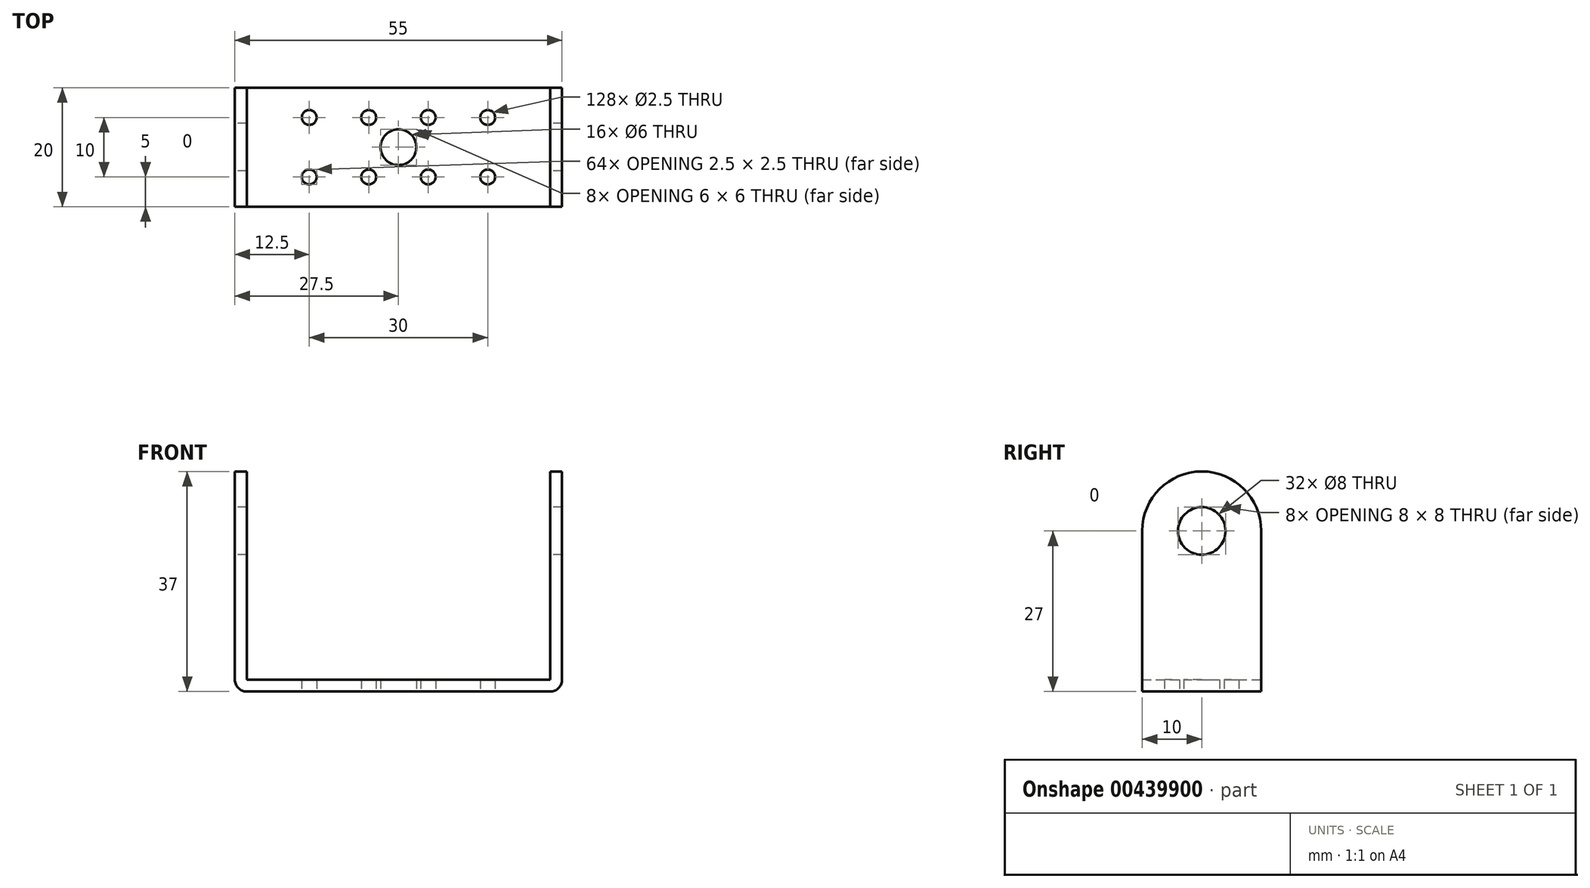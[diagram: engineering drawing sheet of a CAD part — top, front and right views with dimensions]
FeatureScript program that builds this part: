
annotation { "Feature Type Name" : "Feature", "Feature Type Description" : "" }
export const myFeature = defineFeature(function(context is Context, id is Id, definition is map)
    precondition{}
    {
        {
            var Q0;
            Q0=qCreatedBy(makeId("Front.planeOp"),FACE);
            var sketch = newSketch(context, id + "F0", { "sketchPlane" : qUnion([Q0])});
            skLineSegment(sketch, "E0.bottom", {"start": v(-27.5, 37) * mm, "end": v(-25.5, 37) * mm});
            skLineSegment(sketch, "E0.top", {"start": v(-25.5, 2) * mm, "end": v(25.5, 2) * mm});
            skLineSegment(sketch, "E0.left", {"start": v(-25.5, 37) * mm, "end": v(-25.5, 2) * mm});
            skLineSegment(sketch, "E0.right", {"start": v(25.5, 37) * mm, "end": v(25.5, 2) * mm});
            skLineSegment(sketch, "E1", {"start": v(-27.5, 37) * mm, "end": v(-27.5, 0) * mm});
            skLineSegment(sketch, "E2", {"start": v(27.5, 37) * mm, "end": v(27.5, 0) * mm});
            skLineSegment(sketch, "E3.trimOffspring", {"start": v(25.5, 37) * mm, "end": v(27.5, 37) * mm});
            skLineSegment(sketch, "E4", {"start": v(-27.5, 0) * mm, "end": v(27.5, 0) * mm});
            skSolve(sketch);
        }
        {
            var Q0;
            Q0 = qSketchRegion(id + "F0", true);
            extrude(context, id + "F1", {"entities" : qUnion([Q0]), "depth" : 20 * mm});
        }
        {
            var Q0;
            Q0=makeQuery(id+"F1.opExtrude","SWEPT_FACE",FACE,{"disambiguationData":[OSD([sQuery(id+"F0.wireOp",EDGE,"E1")])]});
            var sketch = newSketch(context, id + "F2", { "sketchPlane" : qUnion([Q0])});
            skCircle(sketch, "E5", {"center": v(10, 27) * mm, "radius": 4 * mm});
            skSolve(sketch);
        }
        {
            var Q0;
            Q0 = qSketchRegion(id + "F2", true);
            extrude(context, id + "F3", {"entities" : qUnion([Q0]), "operationType" : NewBodyOperationType.REMOVE, "oppositeDirection" : true, "depth" : 65.2 * mm});
        }
        {
            var Q0;
            Q0=makeQuery(id+"F1.opExtrude","CAP_EDGE",EDGE,{"disambiguationData":[OSD([sQuery(id+"F0.wireOp",EDGE,"E0.bottom")])],"isStart":true});
            var Q1;
            Q1=makeQuery(id+"F1.opExtrude","CAP_EDGE",EDGE,{"disambiguationData":[OSD([sQuery(id+"F0.wireOp",EDGE,"E0.bottom")])],"isStart":false});
            var Q2;
            Q2=makeQuery(id+"F1.opExtrude","CAP_EDGE",EDGE,{"disambiguationData":[OSD([sQuery(id+"F0.wireOp",EDGE,"E3.trimOffspring")])],"isStart":true});
            var Q3;
            Q3=makeQuery(id+"F1.opExtrude","CAP_EDGE",EDGE,{"disambiguationData":[OSD([sQuery(id+"F0.wireOp",EDGE,"E3.trimOffspring")])],"isStart":false});
            fillet(context, id + "F4", {"entities" : qUnion([Q0, Q1, Q2, Q3]), "radius" : 10 * mm, "tangentPropagation" : true, "allowEdgeOverflow" : false});
        }
        {
            var Q0;
            Q0=makeQuery(id+"F1.opExtrude","SWEPT_EDGE",EDGE,{"disambiguationData":[OSD([sQuery(id+"F0.wireOp",EDGE,"E1"),sQuery(id+"F0.wireOp",EDGE,"E4")])]});
            var Q1;
            Q1=makeQuery(id+"F1.opExtrude","SWEPT_EDGE",EDGE,{"disambiguationData":[OSD([sQuery(id+"F0.wireOp",EDGE,"E2"),sQuery(id+"F0.wireOp",EDGE,"E4")])]});
            fillet(context, id + "F5", {"entities" : qUnion([Q0, Q1]), "radius" : 2 * mm, "tangentPropagation" : true, "allowEdgeOverflow" : false});
        }
        {
            var Q0;
            Q0=makeQuery(id+"F1.opExtrude","SWEPT_FACE",FACE,{"disambiguationData":[OSD([sQuery(id+"F0.wireOp",EDGE,"E4")])]});
            var sketch = newSketch(context, id + "F6", { "sketchPlane" : qUnion([Q0])});
            skCircle(sketch, "E6", {"center": v(-15, 15) * mm, "radius": 1.24 * mm});
            skCircle(sketch, "E7.0.1.0", {"center": v(-15, 5) * mm, "radius": 1.24 * mm});
            skCircle(sketch, "E7.1.0.0", {"center": v(-5, 15) * mm, "radius": 1.24 * mm});
            skCircle(sketch, "E7.1.1.0", {"center": v(-5, 5) * mm, "radius": 1.24 * mm});
            skCircle(sketch, "E7.2.0.0", {"center": v(5, 15) * mm, "radius": 1.24 * mm});
            skCircle(sketch, "E7.2.1.0", {"center": v(5, 5) * mm, "radius": 1.24 * mm});
            skCircle(sketch, "E7.3.0.0", {"center": v(15, 15) * mm, "radius": 1.24 * mm});
            skCircle(sketch, "E7.3.1.0", {"center": v(15, 5) * mm, "radius": 1.24 * mm});
            skCircle(sketch, "E8", {"center": v(0, 10) * mm, "radius": 3 * mm});
            skSolve(sketch);
        }
        {
            var Q0;
            Q0=sQuery(id+"F6.wireOp",VERTEX,"E6.center");
            var Q1;
            Q1=sQuery(id+"F6.wireOp",VERTEX,"E7.1.0.0.center");
            var Q2;
            Q2=sQuery(id+"F6.wireOp",VERTEX,"E7.2.0.0.center");
            var Q3;
            Q3=sQuery(id+"F6.wireOp",VERTEX,"E7.3.0.0.center");
            var Q4;
            Q4=sQuery(id+"F6.wireOp",VERTEX,"E7.0.1.0.center");
            var Q5;
            Q5=sQuery(id+"F6.wireOp",VERTEX,"E7.1.1.0.center");
            var Q6;
            Q6=sQuery(id+"F6.wireOp",VERTEX,"E7.2.1.0.center");
            var Q7;
            Q7=sQuery(id+"F6.wireOp",VERTEX,"E7.3.1.0.center");
            var Q8;
            Q8=makeQuery(id+"F1.opExtrude","SWEPT_BODY",BODY,{"disambiguationData":[OSD([sQuery(id+"F0.wireOp",EDGE,"E0.bottom"),sQuery(id+"F0.wireOp",EDGE,"E0.top"),sQuery(id+"F0.wireOp",EDGE,"E0.left"),sQuery(id+"F0.wireOp",EDGE,"E0.right"),sQuery(id+"F0.wireOp",EDGE,"E1"),sQuery(id+"F0.wireOp",EDGE,"E2"),sQuery(id+"F0.wireOp",EDGE,"E3.trimOffspring"),sQuery(id+"F0.wireOp",EDGE,"E4")])]});
            hole(context, id + "F7", {"style" : HoleStyle.SIMPLE, "endStyle" : HoleEndStyle.THROUGH, "holeDiameter" : 2.5 * mm, "isTappedThrough" : true, "tappedDepth" : 12 * mm, "tapClearance" : 3, "startFromSketch" : true, "locations" : qUnion([Q0, Q1, Q2, Q3, Q4, Q5, Q6, Q7]), "scope" : qUnion([Q8])});
        }
        {
            var Q0;
            Q0=sQuery(id+"F6.wireOp",VERTEX,"E8.center");
            var Q1;
            Q1=makeQuery(id+"F1.opExtrude","SWEPT_BODY",BODY,{"disambiguationData":[OSD([sQuery(id+"F0.wireOp",EDGE,"E0.bottom"),sQuery(id+"F0.wireOp",EDGE,"E0.top"),sQuery(id+"F0.wireOp",EDGE,"E0.left"),sQuery(id+"F0.wireOp",EDGE,"E0.right"),sQuery(id+"F0.wireOp",EDGE,"E1"),sQuery(id+"F0.wireOp",EDGE,"E2"),sQuery(id+"F0.wireOp",EDGE,"E3.trimOffspring"),sQuery(id+"F0.wireOp",EDGE,"E4")])]});
            hole(context, id + "F8", {"style" : HoleStyle.SIMPLE, "endStyle" : HoleEndStyle.THROUGH, "holeDiameter" : 6 * mm, "isTappedThrough" : true, "tappedDepth" : 12 * mm, "tapClearance" : 3, "startFromSketch" : true, "locations" : qUnion([Q0]), "scope" : qUnion([Q1])});
        }
    });
